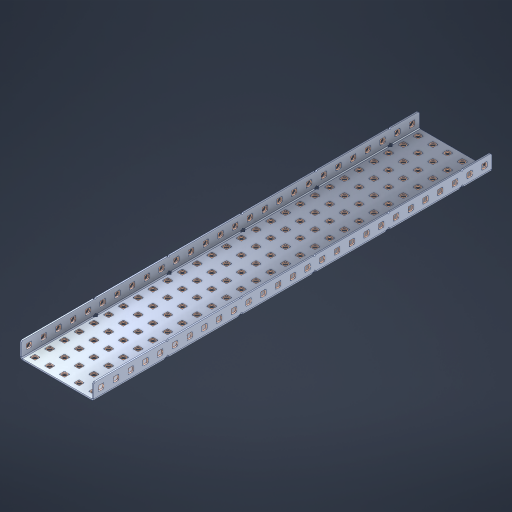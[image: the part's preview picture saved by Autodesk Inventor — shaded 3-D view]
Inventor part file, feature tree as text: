
AUTODESK INVENTOR PART (.ipt)
format: ipt  version: 2023 (Build 270158000, 158)  size: 2,104,832 bytes
history: native  units: in
note: dims shown in document units (in); Inventor stores cm internally (conversion verified against a paired STEP export)
features: other x194, extrude x188, sheet_metal_op x10, sketch x8, mirror x1, pattern_linear x1, chamfer x1
ambient origin geometry x8: Origin, YZ Plane, XZ Plane, XY Plane, X Axis, Y Axis, Z Axis, Center Point
bodies: Solid1 (feature_tree), Body (feature_tree)
feature tree (403):
  other  "Flange Pattern Plane"
  sheet_metal_op  "Flange Pattern"
  sheet_metal_op  "Body Pattern"
  other  "Arc Length"
  mirror  "Notch Mirror"
  pattern_linear  "Notch Pattern"  Spacing1=0.1875in  [1 undecoded]
  chamfer  "End Chamfer"
  extrude  "Half Cut"  Depth=0.0469in
  sketch  "Sketch1"  dims[d0=2.5in]
  other  "Plate1"
  sketch  "Sketch2"  dims[d1=13.5in]
  other  "Plate2"
  sheet_metal_op  "Bend1"
  sheet_metal_op  "Corner1"
  sketch  "Sketch3"  dims[d2=0.0469in]
  other  "Flange Pattern Sketch"
  sketch  "Sketch7"  dims[d3=0.0469in]
  other  "Srf1"
  other  "Srf2"
  sketch  "Sketch8"  dims[d4=0.0234in]
  sketch  "Sketch9"  dims[d5=0.0938in]
  other  "Srf91"
  sheet_metal_op  "Body Pattern Sketch"
  other  "Srf92"
  sketch  "Sketch13"  dims[d6=0.0469in]
  sketch  "Sketch14"  dims[d7=0.5in d8=90.0deg d9=0.0312in d10=0.1875in d11=0.0469in d12=0.0469in d16=0.182in d17=0.02in d18=0.0469in d19=0.0in d20=0.25in d21=0.25in d46=0.172in d47=1.0in d48=0.0in d49=0.182in d50=0.02in d51=0.25in d52=0.25in d53=0.0469in d54=0.0in d55=0.172in d56=1.0in d57=0.0in d60=10.6299in d62=0.5in d63=1.9685in d65=0.5in d85=0.1227in d86=0.1659in d88=0.04in d89=0.0469in d90=0.0in d91=0.04in d92=0.0491in d95=2.5in d96=0.04in d97=0.25in d98=45.0deg d101=0.0in d102=2.497in d131=2.5in d132=10.6299in d134=0.5in d139=0.5in]
  other  "Srf856"
  other  "Srf1310"
  other  "Srf1311"
  other  "Srf1312"
  other  "Srf1376"
  other  "Srf1377"
  other  "Srf1728"
  other  "Srf1755"
  other  "Srf1878"
  other  "Srf1879"
  other  "Srf1880"
  other  "Srf1881"
  other  "Srf1882"
  other  "Srf1883"
  other  "Srf1884"
  other  "Srf1885"
  other  "Srf1886"
  other  "Srf1887"
  other  "Srf1888"
  other  "Srf1889"
  other  "Srf1890"
  other  "Srf1891"
  other  "Srf1892"
  other  "Srf1893"
  other  "Srf1894"
  other  "Srf1895"
  other  "Srf1896"
  other  "Srf1897"
  other  "Srf1898"
  other  "Srf1899"
  other  "Srf1900"
  other  "Srf1901"
  other  "Srf1902"
  other  "Srf1903"
  other  "Srf1904"
  other  "Srf1905"
  other  "Srf1906"
  other  "Srf1942"
  other  "Srf1943"
  other  "Srf1944"
  other  "Srf1945"
  other  "Srf1946"
  other  "Srf1947"
  other  "Srf1948"
  other  "Srf1949"
  other  "Srf1950"
  other  "Srf1951"
  other  "Srf1952"
  other  "Srf1953"
  other  "Srf1954"
  other  "Srf1955"
  other  "Srf1956"
  other  "Srf1957"
  other  "Srf1958"
  other  "Srf1959"
  other  "Srf1960"
  other  "Srf1961"
  other  "Srf1962"
  other  "Srf1963"
  other  "Srf1964"
  other  "Srf1965"
  other  "Srf1966"
  other  "Srf1967"
  other  "Srf1968"
  other  "Srf1969"
  other  "Srf1970"
  other  "Srf2111"
  other  "Srf2112"
  other  "Srf2113"
  other  "Srf2114"
  other  "Srf2115"
  other  "Srf2116"
  other  "Srf2117"
  other  "Srf2118"
  other  "Srf2119"
  other  "Srf2120"
  other  "Srf2121"
  other  "Srf2122"
  other  "Srf2123"
  other  "Srf2124"
  other  "Srf2125"
  other  "Srf2126"
  other  "Srf2127"
  other  "Srf2128"
  other  "Srf2129"
  other  "Srf2146"
  other  "Srf2147"
  other  "Srf2148"
  other  "Srf2149"
  other  "Srf2150"
  other  "Srf2151"
  other  "Srf2152"
  other  "Srf2153"
  other  "Srf2154"
  other  "Srf2155"
  other  "Srf2156"
  other  "Srf2157"
  other  "Srf2158"
  other  "Srf2159"
  other  "Srf2160"
  other  "Srf2161"
  other  "Srf2162"
  other  "Srf2163"
  other  "Srf2164"
  other  "Srf2165"
  other  "Srf2166"
  other  "Srf2167"
  other  "Srf2168"
  other  "Srf2169"
  other  "Srf2170"
  other  "Srf2171"
  other  "Srf2172"
  other  "Srf2173"
  other  "Srf2174"
  other  "Srf2175"
  other  "Srf2176"
  other  "Srf2177"
  other  "Srf2178"
  other  "Srf2179"
  other  "Srf2180"
  other  "Srf2181"
  other  "Srf2182"
  other  "Srf2183"
  other  "Srf2184"
  other  "Srf2185"
  other  "Srf2186"
  other  "Srf2187"
  other  "Srf2188"
  other  "Srf2189"
  other  "Srf2190"
  other  "Srf2191"
  other  "Srf2192"
  other  "Srf2193"
  other  "Srf2194"
  other  "Srf2195"
  other  "Srf2196"
  other  "Srf2197"
  other  "Srf2198"
  other  "Srf2199"
  other  "Srf2200"
  other  "Srf2201"
  other  "Srf2202"
  other  "Srf2203"
  other  "Srf2204"
  other  "Srf2205"
  other  "Srf2206"
  other  "Srf2207"
  other  "Srf2208"
  other  "Srf2209"
  other  "Srf2210"
  other  "Srf2211"
  other  "Srf2212"
  other  "Srf2213"
  other  "Srf2214"
  other  "Srf2215"
  other  "Srf2216"
  other  "Srf2217"
  other  "Srf2218"
  other  "Srf2219"
  other  "Srf2220"
  other  "Srf2221"
  other  "Srf2222"
  other  "Srf2223"
  other  "Srf2224"
  other  "Srf2225"
  other  "Srf2226"
  other  "Srf2227"
  other  "Srf2228"
  other  "Srf2229"
  other  "Srf2230"
  other  "Srf2231"
  other  "Srf2232"
  other  "Srf2233"
  other  "Srf2234"
  other  "Srf2235"
  other  "Srf2236"
  other  "Srf2237"
  other  "Srf2238"
  other  "Srf2239"
  other  "Srf2240"
  other  "Srf2241"
  other  "Srf2242"
  other  "Srf2243"
  other  "Srf2244"
  other  "Srf2245"
  sheet_metal_op  "Flange Stamp"
  sheet_metal_op  "Flange Circle"
  sheet_metal_op  "Body Stamp"
  sheet_metal_op  "Body Circle"
  sheet_metal_op  "Notch"
  extrude  "ExtrusionSrf2"  Depth=0.0469in
  extrude  "ExtrusionSrf92"  Depth=2.5in
  extrude  "ExtrusionSrf856"  Depth=0.02in
  extrude  "ExtrusionSrf1310"  Depth=0.0469in
  extrude  "ExtrusionSrf1311"  TaperAngle=0.0deg  [1 undecoded]
  extrude  "ExtrusionSrf1312"  Depth=0.25in
  extrude  "ExtrusionSrf1376"  Depth=0.25in
  extrude  "ExtrusionSrf1377"  Depth=2.5in
  extrude  "ExtrusionSrf1728"  Depth=2.5in TaperAngle=0.0deg
  extrude  "ExtrusionSrf1755"  Depth=2.5in
  extrude  "ExtrusionSrf1878"  Depth=0.02in
  extrude  "ExtrusionSrf1879"  Depth=0.25in
  extrude  "ExtrusionSrf1880"  Depth=0.25in
  extrude  "ExtrusionSrf1881"  Depth=0.0469in
  extrude  "ExtrusionSrf1882"  TaperAngle=0.0deg  [1 undecoded]
  extrude  "ExtrusionSrf1883"  Depth=2.5in
  extrude  "ExtrusionSrf1884"  Depth=2.5in TaperAngle=0.0deg
  extrude  "ExtrusionSrf1885"  Depth=2.5in
  extrude  "ExtrusionSrf1886"  Depth=2.5in
  extrude  "ExtrusionSrf1887"  Depth=2.5in
  extrude  "ExtrusionSrf1888"  Depth=2.5in
  extrude  "ExtrusionSrf1889"  Depth=2.5in
  extrude  "ExtrusionSrf1890"  Depth=0.0469in
  extrude  "ExtrusionSrf1891"  TaperAngle=0.0deg  [1 undecoded]
  extrude  "ExtrusionSrf1892"  Depth=2.5in
  extrude  "ExtrusionSrf1893"  Depth=2.5in
  extrude  "ExtrusionSrf1894"  Depth=2.5in
  extrude  "ExtrusionSrf1895"  Depth=0.25in TaperAngle=45.0deg
  extrude  "ExtrusionSrf1896"  TaperAngle=0.0deg  [1 undecoded]
  extrude  "ExtrusionSrf1897"  Depth=2.5in
  extrude  "ExtrusionSrf1898"  Depth=2.5in
  extrude  "ExtrusionSrf1899"  Depth=2.5in
  extrude  "ExtrusionSrf1900"  Depth=2.5in
  extrude  "ExtrusionSrf1901"  Depth=2.5in
  extrude  "ExtrusionSrf1902"  [1 undecoded]
  extrude  "ExtrusionSrf1903"  [1 undecoded]
  extrude  "ExtrusionSrf1904"  [1 undecoded]
  extrude  "ExtrusionSrf1905"  [1 undecoded]
  extrude  "ExtrusionSrf1906"  [1 undecoded]
  extrude  "ExtrusionSrf1942"  [1 undecoded]
  extrude  "ExtrusionSrf1943"  [1 undecoded]
  extrude  "ExtrusionSrf1944"  [1 undecoded]
  extrude  "ExtrusionSrf1945"  [1 undecoded]
  extrude  "ExtrusionSrf1946"  [1 undecoded]
  extrude  "ExtrusionSrf1947"  [1 undecoded]
  extrude  "ExtrusionSrf1948"  [1 undecoded]
  extrude  "ExtrusionSrf1949"  [1 undecoded]
  extrude  "ExtrusionSrf1950"  [1 undecoded]
  extrude  "ExtrusionSrf1951"  [1 undecoded]
  extrude  "ExtrusionSrf1952"  [1 undecoded]
  extrude  "ExtrusionSrf1953"  [1 undecoded]
  extrude  "ExtrusionSrf1954"  [1 undecoded]
  extrude  "ExtrusionSrf1955"  [1 undecoded]
  extrude  "ExtrusionSrf1956"  [1 undecoded]
  extrude  "ExtrusionSrf1957"  [1 undecoded]
  extrude  "ExtrusionSrf1958"  [1 undecoded]
  extrude  "ExtrusionSrf1959"  [1 undecoded]
  extrude  "ExtrusionSrf1960"  [1 undecoded]
  extrude  "ExtrusionSrf1961"  [1 undecoded]
  extrude  "ExtrusionSrf1962"  [1 undecoded]
  extrude  "ExtrusionSrf1963"  [1 undecoded]
  extrude  "ExtrusionSrf1964"  [1 undecoded]
  extrude  "ExtrusionSrf1965"  [1 undecoded]
  extrude  "ExtrusionSrf1966"  [1 undecoded]
  extrude  "ExtrusionSrf1967"  [1 undecoded]
  extrude  "ExtrusionSrf1968"  [1 undecoded]
  extrude  "ExtrusionSrf1969"  [1 undecoded]
  extrude  "ExtrusionSrf1970"  [1 undecoded]
  extrude  "ExtrusionSrf2111"  [1 undecoded]
  extrude  "ExtrusionSrf2112"  [1 undecoded]
  extrude  "ExtrusionSrf2113"  [1 undecoded]
  extrude  "ExtrusionSrf2114"  [1 undecoded]
  extrude  "ExtrusionSrf2115"  [1 undecoded]
  extrude  "ExtrusionSrf2116"  [1 undecoded]
  extrude  "ExtrusionSrf2117"  [1 undecoded]
  extrude  "ExtrusionSrf2118"  [1 undecoded]
  extrude  "ExtrusionSrf2119"  [1 undecoded]
  extrude  "ExtrusionSrf2120"  [1 undecoded]
  extrude  "ExtrusionSrf2121"  [1 undecoded]
  extrude  "ExtrusionSrf2122"  [1 undecoded]
  extrude  "ExtrusionSrf2123"  [1 undecoded]
  extrude  "ExtrusionSrf2124"  [1 undecoded]
  extrude  "ExtrusionSrf2125"  [1 undecoded]
  extrude  "ExtrusionSrf2126"  [1 undecoded]
  extrude  "ExtrusionSrf2127"  [1 undecoded]
  extrude  "ExtrusionSrf2128"  [1 undecoded]
  extrude  "ExtrusionSrf2129"  [1 undecoded]
  extrude  "ExtrusionSrf2146"  [1 undecoded]
  extrude  "ExtrusionSrf2147"  [1 undecoded]
  extrude  "ExtrusionSrf2148"  [1 undecoded]
  extrude  "ExtrusionSrf2149"  [1 undecoded]
  extrude  "ExtrusionSrf2150"  [1 undecoded]
  extrude  "ExtrusionSrf2151"  [1 undecoded]
  extrude  "ExtrusionSrf2152"  [1 undecoded]
  extrude  "ExtrusionSrf2153"  [1 undecoded]
  extrude  "ExtrusionSrf2154"  [1 undecoded]
  extrude  "ExtrusionSrf2155"  [1 undecoded]
  extrude  "ExtrusionSrf2156"  [1 undecoded]
  extrude  "ExtrusionSrf2157"  [1 undecoded]
  extrude  "ExtrusionSrf2158"  [1 undecoded]
  extrude  "ExtrusionSrf2159"  [1 undecoded]
  extrude  "ExtrusionSrf2160"  [1 undecoded]
  extrude  "ExtrusionSrf2161"  [1 undecoded]
  extrude  "ExtrusionSrf2162"  [1 undecoded]
  extrude  "ExtrusionSrf2163"  [1 undecoded]
  extrude  "ExtrusionSrf2164"  [1 undecoded]
  extrude  "ExtrusionSrf2165"  [1 undecoded]
  extrude  "ExtrusionSrf2166"  [1 undecoded]
  extrude  "ExtrusionSrf2167"  [1 undecoded]
  extrude  "ExtrusionSrf2168"  [1 undecoded]
  extrude  "ExtrusionSrf2169"  [1 undecoded]
  extrude  "ExtrusionSrf2170"  [1 undecoded]
  extrude  "ExtrusionSrf2171"  [1 undecoded]
  extrude  "ExtrusionSrf2172"  [1 undecoded]
  extrude  "ExtrusionSrf2173"  [1 undecoded]
  extrude  "ExtrusionSrf2174"  [1 undecoded]
  extrude  "ExtrusionSrf2175"  [1 undecoded]
  extrude  "ExtrusionSrf2176"  [1 undecoded]
  extrude  "ExtrusionSrf2177"  [1 undecoded]
  extrude  "ExtrusionSrf2178"  [1 undecoded]
  extrude  "ExtrusionSrf2179"  [1 undecoded]
  extrude  "ExtrusionSrf2180"  [1 undecoded]
  extrude  "ExtrusionSrf2181"  [1 undecoded]
  extrude  "ExtrusionSrf2182"  [1 undecoded]
  extrude  "ExtrusionSrf2183"  [1 undecoded]
  extrude  "ExtrusionSrf2184"  [1 undecoded]
  extrude  "ExtrusionSrf2185"  [1 undecoded]
  extrude  "ExtrusionSrf2186"  [1 undecoded]
  extrude  "ExtrusionSrf2187"  [1 undecoded]
  extrude  "ExtrusionSrf2188"  [1 undecoded]
  extrude  "ExtrusionSrf2189"  [1 undecoded]
  extrude  "ExtrusionSrf2190"  [1 undecoded]
  extrude  "ExtrusionSrf2191"  [1 undecoded]
  extrude  "ExtrusionSrf2192"  [1 undecoded]
  extrude  "ExtrusionSrf2193"  [1 undecoded]
  extrude  "ExtrusionSrf2194"  [1 undecoded]
  extrude  "ExtrusionSrf2195"  [1 undecoded]
  extrude  "ExtrusionSrf2196"  [1 undecoded]
  extrude  "ExtrusionSrf2197"  [1 undecoded]
  extrude  "ExtrusionSrf2198"  [1 undecoded]
  extrude  "ExtrusionSrf2199"  [1 undecoded]
  extrude  "ExtrusionSrf2200"  [1 undecoded]
  extrude  "ExtrusionSrf2201"  [1 undecoded]
  extrude  "ExtrusionSrf2202"  [1 undecoded]
  extrude  "ExtrusionSrf2203"  [1 undecoded]
  extrude  "ExtrusionSrf2204"  [1 undecoded]
  extrude  "ExtrusionSrf2205"  [1 undecoded]
  extrude  "ExtrusionSrf2206"  [1 undecoded]
  extrude  "ExtrusionSrf2207"  [1 undecoded]
  extrude  "ExtrusionSrf2208"  [1 undecoded]
  extrude  "ExtrusionSrf2209"  [1 undecoded]
  extrude  "ExtrusionSrf2210"  [1 undecoded]
  extrude  "ExtrusionSrf2211"  [1 undecoded]
  extrude  "ExtrusionSrf2212"  [1 undecoded]
  extrude  "ExtrusionSrf2213"  [1 undecoded]
  extrude  "ExtrusionSrf2214"  [1 undecoded]
  extrude  "ExtrusionSrf2215"  [1 undecoded]
  extrude  "ExtrusionSrf2216"  [1 undecoded]
  extrude  "ExtrusionSrf2217"  [1 undecoded]
  extrude  "ExtrusionSrf2218"  [1 undecoded]
  extrude  "ExtrusionSrf2219"  [1 undecoded]
  extrude  "ExtrusionSrf2220"  [1 undecoded]
  extrude  "ExtrusionSrf2221"  [1 undecoded]
  extrude  "ExtrusionSrf2222"  [1 undecoded]
  extrude  "ExtrusionSrf2223"  [1 undecoded]
  extrude  "ExtrusionSrf2224"  [1 undecoded]
  extrude  "ExtrusionSrf2225"  [1 undecoded]
  extrude  "ExtrusionSrf2226"  [1 undecoded]
  extrude  "ExtrusionSrf2227"  [1 undecoded]
  extrude  "ExtrusionSrf2228"  [1 undecoded]
  extrude  "ExtrusionSrf2229"  [1 undecoded]
  extrude  "ExtrusionSrf2230"  [1 undecoded]
  extrude  "ExtrusionSrf2231"  [1 undecoded]
  extrude  "ExtrusionSrf2232"  [1 undecoded]
  extrude  "ExtrusionSrf2233"  [1 undecoded]
  extrude  "ExtrusionSrf2234"  [1 undecoded]
  extrude  "ExtrusionSrf2235"  [1 undecoded]
  extrude  "ExtrusionSrf2236"  [1 undecoded]
  extrude  "ExtrusionSrf2237"  [1 undecoded]
  extrude  "ExtrusionSrf2238"  [1 undecoded]
  extrude  "ExtrusionSrf2239"  [1 undecoded]
  extrude  "ExtrusionSrf2240"  [1 undecoded]
  extrude  "ExtrusionSrf2241"  [1 undecoded]
  extrude  "ExtrusionSrf2242"  [1 undecoded]
  extrude  "ExtrusionSrf2243"  [1 undecoded]
  extrude  "ExtrusionSrf2244"  [1 undecoded]
  extrude  "ExtrusionSrf2245"  [1 undecoded]
note: 158 required parameter values undecoded (feature->parameter linkage not recoverable at this tier; creation-order binding heuristic only, values carry confidence <= 0.55)
